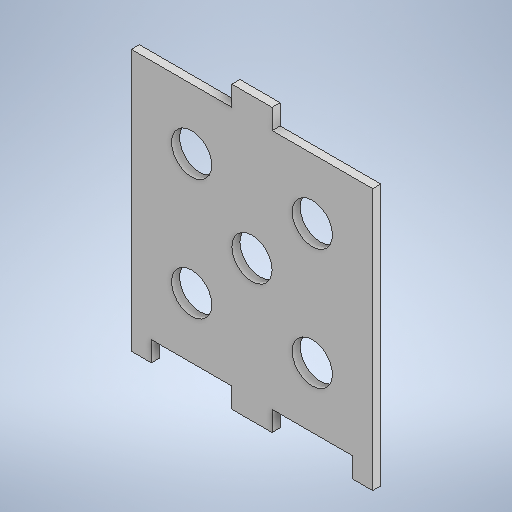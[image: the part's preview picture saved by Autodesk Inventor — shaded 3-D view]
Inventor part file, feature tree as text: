
AUTODESK INVENTOR PART (.ipt)
format: ipt  version: 2025.1 (Build 291241020, 241B)  size: 283,136 bytes
history: native  units: in
note: dims shown in document units (in); Inventor stores cm internally (conversion verified against a paired STEP export)
features: extrude x2, sketch x2
ambient origin geometry x8: Origin, YZ Plane, XZ Plane, XY Plane, X Axis, Y Axis, Z Axis, Center Point
bodies: Solid1 (feature_tree)
feature tree (4):
  extrude  "Extrusion1"  Depth=6.0in
  extrude  "Extrusion2"  Depth=0.5in
  sketch  "Sketch1"  dims[d0=6.0in d1=6.0in]
  sketch  "Sketch2"  dims[d5=0.5in d6=0.5in d7=0.5in d8=0.5in d9=2.5in d10=90.0deg d11=1.0in d12=1.0in d13=1.0in d14=1.0in d15=1.0in d16=1.5in d17=1.5in d18=1.5in d19=1.5in d20=3.0in d21=3.0in d22=1.5in d23=1.5in d24=1.5in d25=1.5in d26=0.5in d27=0.2in d28=0.0in d29=0.5in d31=0.5in d32=0.5in d33=0.0in]
